# Revit family: EC-11-TY5137_Imperial
name_source: partatom
category: Sprinklers
units: mm (PartAtom-declared; Revit-internal decimal feet)

## family parameters
Always vertical = Yes
Cut with Voids When Loaded = No
Maintain Annotation Orientation = No
OmniClass Number = 23.65.70.17.11.24
OmniClass Title = Fire Fighting Sprinkler Heads
Part Type = Normal
Room Calculation Point = No
Round Connector Dimension = Use Diameter
Shared = No
Work Plane-Based = No

## types (22) — shared parameters
COBie = Yes
COBie.Component.Name = Sprinklers:Upright_SIN
COBie.Type = Yes
COBie.Type.AssetType = Fixed
COBie.Type.Category = Pr_70_55_97_84:Sprinklers
COBie.Type.DurationUnit = year
COBie.Type.Manufacturer = Tyco Fire Protection Products
COBie.Type.Material = Bronze
COBie.Type.NominalHeight = 0' - 0"
COBie.Type.NominalLength = 0' - 0"
COBie.Type.NominalWidth = 0' - 0"
COBie.Type.Shape = Cylinder
COBie.Type.Size = 3/4"(DN20)
COBie.Type.WarrantyGuarantorParts = http://tycofsbp.com
Coverage = Extended
Coverage_ = Extended
Default Elevation = 0' - 0"
K-Factor = 11.0986
Manufacturer = Tyco Fire Protection Products
Manufacturer URL = www.tyco-fire.com
Material_ = Bronze
Model = EC-11
Nominal Diameter 1 = 1"
Orifice = Extra Large
Orifice Size = 0"
Outside Diameter 1 = 1"
Response = Quick
Response_ = Quick
SIN No = TY5137
Takeout 1 = 2"
Technical Data Sheet No = TFP220
zero-valued in all types: COBie.Type.ReplacementCost, Style Id

## per-type parameters (varying)
| type | COBie.Component.Description | COBie.Type.Colour | COBie.Type.Finish | COBie.Type.ModelNumber | COBie.Type.ModelReference | Description | Finish_ | Part No | Temperature Rating |
| EC-11 Wet Upright_135  57.2°C K160 DN20 NPT Br_51-894-1-135 | EC-11 Wet Upright  57.2°C K160 DN20 NPT Br | Yellow | Natural Brass | 51-894-1-135 | EC-11 Wet Upright  57.2°C K160 DN20 NPT Br | EC-11 Wet Upright_Yellow_135  57.2°C K160 DN20 NPT Br | Natural Brass | 51-894-1-135 | 135 °F |
| EC-11 Wet Upright_155  68.3°C K160 DN20 NPT Br_51-894-1-155 | EC-11 Wet Upright  68.3°C K160 DN20 NPT Br | Yellow | Natural Brass | 51-894-1-155 | EC-11 Wet Upright  68.3°C K160 DN20 NPT Br | EC-11 Wet Upright_Yellow_155  68.3°C K160 DN20 NPT Br | Natural Brass | 51-894-1-155 | 155 °F |
| EC-11 Wet Upright_175  79.4°C K160 DN20 NPT Br_51-894-1-175 | EC-11 Wet Upright  79.4°C K160 DN20 NPT Br | Yellow | Natural Brass | 51-894-1-175 | EC-11 Wet Upright  79.4°C K160 DN20 NPT Br | EC-11 Wet Upright_Yellow_175  79.4°C K160 DN20 NPT Br | Natural Brass | 51-894-1-175 | 175 °F |
| EC-11 Wet Upright_200  93.3°C K160 DN20 NPT Br_51-894-1-200 | EC-11 Wet Upright  93.3°C K160 DN20 NPT Br | Yellow | Natural Brass | 51-894-1-200 | EC-11 Wet Upright  93.3°C K160 DN20 NPT Br | EC-11 Wet Upright_Yellow_200  93.3°C K160 DN20 NPT Br | Natural Brass | 51-894-1-200 | 200 °F |
| EC-11 Wet Upright_286  141.1°C K160 DN20 NPT Br_51-894-1-286 | EC-11 Wet Upright  141.1°C K160 DN20 NPT Br | Yellow | Natural Brass | 51-894-1-286 | EC-11 Wet Upright  141.1°C K160 DN20 NPT Br | EC-11 Wet Upright_Yellow_286  141.1°C K160 DN20 NPT Br | Natural Brass | 51-894-1-286 | 286 °F |
| EC-11 Wet Upright_135  57.2°C K160 DN20 NPT Wh9003PE_51-894-4-135 | EC-11 Wet Upright  57.2°C K160 DN20 NPT Wh9003PE | White | Signal White | 51-894-4-135 | EC-11 Wet Upright  57.2°C K160 DN20 NPT Wh9003PE | EC-11 Wet Upright_White_135  57.2°C K160 DN20 NPT Wh9003PE | White RAL9003 | 51-894-4-135 | 135 °F |
| EC-11 Wet Upright_155  68.3°C K160 DN20 NPT Wh9003PE_51-894-4-155 | EC-11 Wet Upright  68.3°C K160 DN20 NPT Wh9003PE | White | Signal White | 51-894-4-155 | EC-11 Wet Upright  68.3°C K160 DN20 NPT Wh9003PE | EC-11 Wet Upright_White_155  68.3°C K160 DN20 NPT Wh9003PE | White RAL9003 | 51-894-4-155 | 155 °F |
| EC-11 Wet Upright_175  79.4°C K160 DN20 NPT Wh9003PE_51-894-4-175 | EC-11 Wet Upright  79.4°C K160 DN20 NPT Wh9003PE | White | Signal White | 51-894-4-175 | EC-11 Wet Upright  79.4°C K160 DN20 NPT Wh9003PE | EC-11 Wet Upright_White_175  79.4°C K160 DN20 NPT Wh9003PE | White RAL9003 | 51-894-4-175 | 175 °F |
| EC-11 Wet Upright_200  93.3°C K160 DN20 NPT Wh9003PE_51-894-4-200 | EC-11 Wet Upright  93.3°C K160 DN20 NPT Wh9003PE | White | Signal White | 51-894-4-200 | EC-11 Wet Upright  93.3°C K160 DN20 NPT Wh9003PE | EC-11 Wet Upright_White_200  93.3°C K160 DN20 NPT Wh9003PE | White RAL9003 | 51-894-4-200 | 200 °F |
| EC-11 Wet Upright_286  141.1°C K160 DN20 NPT Wh9003PE_51-894-4-286 | EC-11 Wet Upright  141.1°C K160 DN20 NPT Wh9003PE | White | Signal White | 51-894-4-286 | EC-11 Wet Upright  141.1°C K160 DN20 NPT Wh9003PE | EC-11 Wet Upright_White_286  141.1°C K160 DN20 NPT Wh9003PE | White RAL9003 | 51-894-4-286 | 286 °F |
| EC-11 Wet Upright_155   68.3°C K160 DN20 NPT JBlk_51-894-5-155 | EC-11 Wet Upright_White_155  68.3°C K160 DN20 NPT Wh9003PE | Black | Jet Black | 51-894-5-155 | EC-11 Wet Upright_White_155  68.3°C K160 DN20 NPT Wh9003PE | EC-11 Wet Upright_Black_155   68.3°C K160 DN20 NPT JBlk | Jet Black RAL9005 | 51-894-5-155 | 155 °F |
| EC-11 Wet Upright_200  68.3°C K160 DN20 NPT JBlk_51-894-5-200 | EC-11 Wet Upright_Black_155   68.3°C K160 DN20 NPT Wh9003PE | Black | Jet Black | 51-894-5-200 | EC-11 Wet Upright_Black_155   68.3°C K160 DN20 NPT Wh9003PE | EC-11 Wet Upright_Black_200  68.3°C K160 DN20 NPT JBlk | Jet Black RAL9005 | 51-894-5-200 | 155 °F |
| EC-11 Wet Upright_135  57.2°C K160 DN20 NPT Lead_51-894-7-135 | EC-11 Wet Upright  57.2°C K160 DN20 NPT LeadCt | Gray | Lead Coated | 51-894-7-135 | EC-11 Wet Upright  57.2°C K160 DN20 NPT LeadCt | EC-11 Wet Upright_Gray_135  57.2°C K160 DN20 NPT Lead | Lead Coated | 51-894-7-135 | 135 °F |
| EC-11 Wet Upright_155  68.3°C K160 DN20 NPT Lead_51-894-7-155 | EC-11 Wet Upright  68.3°C K160 DN20 NPT LeadCt | Gray | Lead Coated | 51-894-7-155 | EC-11 Wet Upright  68.3°C K160 DN20 NPT LeadCt | EC-11 Wet Upright_Gray_155  68.3°C K160 DN20 NPT Lead | Lead Coated | 51-894-7-155 | 155 °F |
| EC-11 Wet Upright_175  79.4°C K160 DN20 NPT Lead_51-894-7-175 | EC-11 Wet Upright  79.4°C K160 DN20 NPT LeadCt | Gray | Lead Coated | 51-894-7-175 | EC-11 Wet Upright  79.4°C K160 DN20 NPT LeadCt | EC-11 Wet Upright_Gray_175  79.4°C K160 DN20 NPT Lead | Lead Coated | 51-894-7-175 | 175 °F |
| EC-11 Wet Upright_200  93.3°C K160 DN20 NPT Lead_51-894-7-200 | EC-11 Wet Upright  93.3°C K160 DN20 NPT LeadCt | Gray | Lead Coated | 51-894-7-200 | EC-11 Wet Upright  93.3°C K160 DN20 NPT LeadCt | EC-11 Wet Upright_Gray_200  93.3°C K160 DN20 NPT Lead | Lead Coated | 51-894-7-200 | 200 °F |
| EC-11 Wet Upright_286  141.1°C K160 DN20 NPT Lead_51-894-7-286 | EC-11 Wet Upright  141.1°C K160 DN20 NPT LeadCt | Gray | Lead Coated | 51-894-7-286 | EC-11 Wet Upright  141.1°C K160 DN20 NPT LeadCt | EC-11 Wet Upright_Gray_286  141.1°C K160 DN20 NPT Lead | Lead Coated | 51-894-7-286 | 286 °F |
| EC-11 Wet Upright_135  57.2°C K160 DN20 NPT Chr_51-894-9-135 | EC-11 Wet Upright  57.2°C K160 DN20 NPT Chr | Silver | Chrome Plated | 51-894-9-135 | EC-11 Wet Upright  57.2°C K160 DN20 NPT Chr | EC-11 Wet Upright_Silver_135  57.2°C K160 DN20 NPT Chr | Chrome Plated | 51-894-9-135 | 135 °F |
| EC-11 Wet Upright_155  68.3°C K160 DN20 NPT Chr_51-894-9-155 | EC-11 Wet Upright  68.3°C K160 DN20 NPT Chr | Silver | Chrome Plated | 51-894-9-155 | EC-11 Wet Upright  68.3°C K160 DN20 NPT Chr | EC-11 Wet Upright_Silver_155  68.3°C K160 DN20 NPT Chr | Chrome Plated | 51-894-9-155 | 155 °F |
| EC-11 Wet Upright_175  79.4°C K160 DN20 NPT Chr_51-894-9-175 | EC-11 Wet Upright  79.4°C K160 DN20 NPT Chr | Silver | Chrome Plated | 51-894-9-175 | EC-11 Wet Upright  79.4°C K160 DN20 NPT Chr | EC-11 Wet Upright_Silver_175  79.4°C K160 DN20 NPT Chr | Chrome Plated | 51-894-9-175 | 175 °F |
| EC-11 Wet Upright_200  93.3°C K160 DN20 NPT Chr_51-894-9-200 | EC-11 Wet Upright  93.3°C K160 DN20 NPT Chr | Silver | Chrome Plated | 51-894-9-200 | EC-11 Wet Upright  93.3°C K160 DN20 NPT Chr | EC-11 Wet Upright_Silver_200  93.3°C K160 DN20 NPT Chr | Chrome Plated | 51-894-9-200 | 200 °F |
| EC-11 Wet Upright_286  141.1°C K160 DN20 NPT Chr_51-894-9-286 | EC-11 Wet Upright  141.1°C K160 DN20 NPT Chr | Silver | Chrome Plated | 51-894-9-286 | EC-11 Wet Upright  141.1°C K160 DN20 NPT Chr | EC-11 Wet Upright_Silver_286  141.1°C K160 DN20 NPT Chr | Chrome Plated | 51-894-9-286 | 286 °F |

## geometry (parser evidence)
native form markers: Blend x2, Sweep x60
no freeform markers — native parametric forms only
